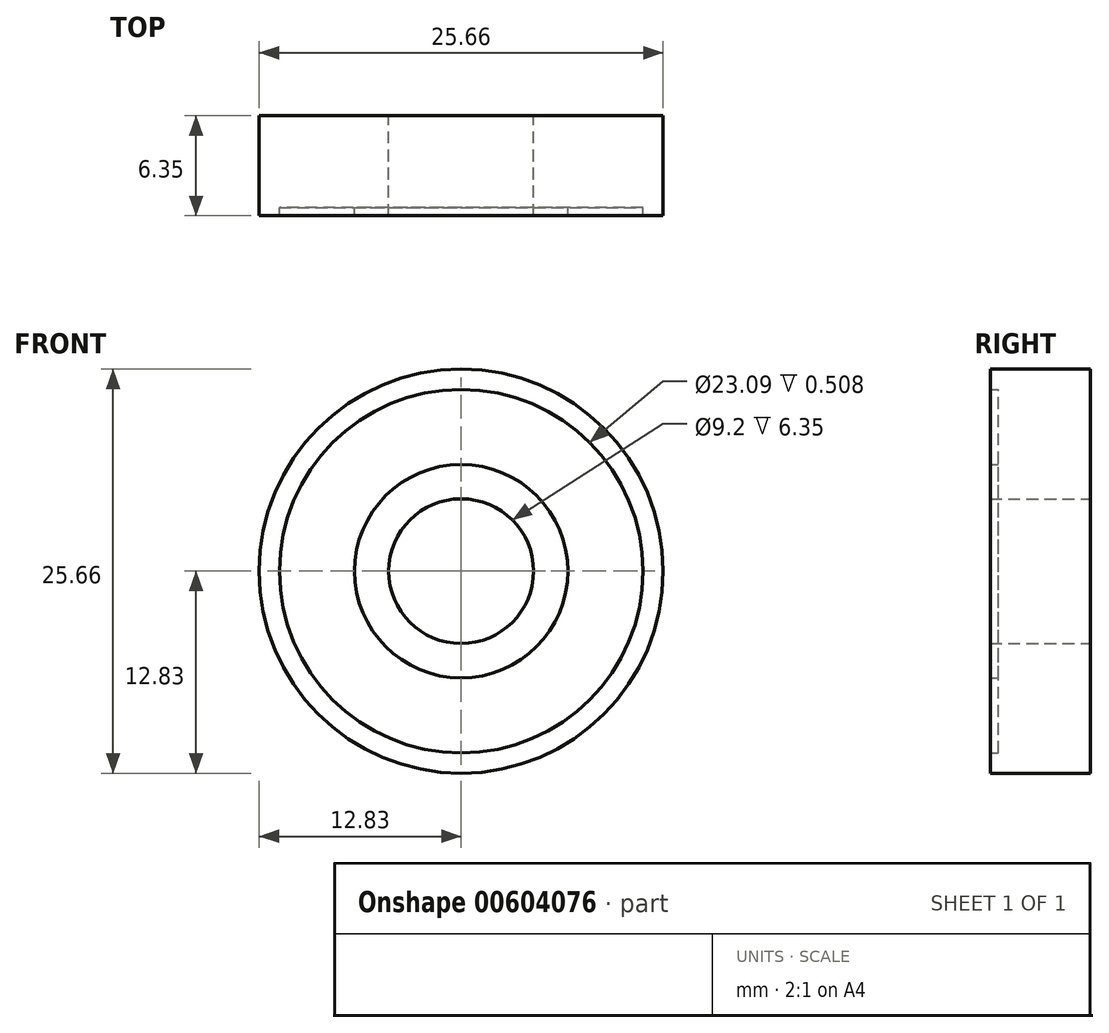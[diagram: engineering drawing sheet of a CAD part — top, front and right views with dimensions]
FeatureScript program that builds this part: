
annotation { "Feature Type Name" : "Feature", "Feature Type Description" : "" }
export const myFeature = defineFeature(function(context is Context, id is Id, definition is map)
    precondition{}
    {
        {
            var Q0;
            Q0=qCreatedBy(makeId("Front.planeOp"),FACE);
            var sketch = newSketch(context, id + "F0", { "sketchPlane" : qUnion([Q0])});
            skCircle(sketch, "E0", {"center": v(0, 0) * mm, "radius": 12.83 * mm});
            skCircle(sketch, "E1", {"center": v(0, 0) * mm, "radius": 11.55 * mm});
            skSolve(sketch);
        }
        {
            var Q0;
            Q0 = qSketchRegion(id + "F0", true);
            extrude(context, id + "F1", {"entities" : qUnion([Q0]), "depth" : 6.35 * mm, "offsetDistance" : 25.4 * mm});
        }
        {
            var Q0;
            Q0=qCreatedBy(makeId("Front.planeOp"),FACE);
            var sketch = newSketch(context, id + "F2", { "sketchPlane" : qUnion([Q0])});
            skCircle(sketch, "E2", {"center": v(0, 0) * mm, "radius": 11.57 * mm});
            skCircle(sketch, "E3", {"center": v(0, 0) * mm, "radius": 6.77 * mm});
            skSolve(sketch);
        }
        {
            var Q0;
            Q0 = qSketchRegion(id + "F2", true);
            extrude(context, id + "F3", {"entities" : qUnion([Q0]), "operationType" : NewBodyOperationType.ADD, "depth" : 5.84 * mm, "offsetDistance" : 25.4 * mm});
        }
        {
            var Q0;
            Q0=qCreatedBy(makeId("Front.planeOp"),FACE);
            var sketch = newSketch(context, id + "F4", { "sketchPlane" : qUnion([Q0])});
            skCircle(sketch, "E4", {"center": v(0, 0) * mm, "radius": 6.78 * mm});
            skCircle(sketch, "E5", {"center": v(0, 0) * mm, "radius": 4.6 * mm});
            skSolve(sketch);
        }
        {
            var Q0;
            Q0 = qSketchRegion(id + "F4", true);
            extrude(context, id + "F5", {"entities" : qUnion([Q0]), "operationType" : NewBodyOperationType.ADD, "depth" : 6.35 * mm, "offsetDistance" : 25.4 * mm});
        }
    });
